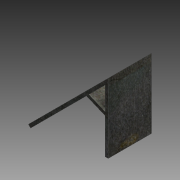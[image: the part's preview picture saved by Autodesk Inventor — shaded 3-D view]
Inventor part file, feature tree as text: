
AUTODESK INVENTOR PART (.ipt)
format: ipt  version: 2016 (Build 200138000, 138)  size: 133,120 bytes
history: native  units: mm
features: extrude x3, sketch x3, projected_geometry x2
ambient origin geometry x8: Origin, YZ Plane, XZ Plane, XY Plane, X Axis, Y Axis, Z Axis, Center Point
bodies: 实体1 (feature_tree)
feature tree (8):
  extrude  "拉伸1"  Depth=3.0mm
  extrude  "拉伸2"  Depth=3.0mm
  extrude  "拉伸3"  Depth=42.0mm TaperAngle=0.0deg
  sketch  "草图1"  dims[d2=45.0deg d3=60.0mm d4=3.0mm]
  sketch  "草图2"  dims[d5=67.5deg d6=3.0mm]
  projected_geometry  "投影回路1"
  sketch  "草图3"  dims[d7=42.0mm d8=0.0mm d9=42.0mm d10=0.0mm d11=30.0mm d12=21.0mm d13=21.0mm d14=42.0mm d15=0.0mm]
  projected_geometry  "投影回路2"
